# Revit family: Keilhauer_Pact_Bench_Tete_A_Tete_77221
name_source: partatom
category: Furniture
revit_build: Autodesk Revit 2017 (Build: 20160225_1515(x64)
units: mm (PartAtom-declared; Revit-internal decimal feet)

## family parameters
Always vertical = Yes
Cut with Voids When Loaded = No
OmniClass Number = 23.40.70.14.64.11
OmniClass Title = Office Furniture
Room Calculation Point = No
Shared = No
Work Plane-Based = No

## types (10) — shared parameters
Assembly Code = E2020200
Catalog = Pact
Manufacturer = Keilhauer, Corp.
Product Documentation Link = http://www.keilhauer.com
URL = http://www.keilhauer.com

## per-type parameters (varying)
| type | Back Left | Back Right | Config | Description | Front Left | Front Right | Length 1 | Model | Size |
| 84" asymmetrical Tete-A-Tete RAF bench | No | Yes | 4 | Pact 84" asymmetrical Tete-A-Tete RAF bench | Yes | No | 40.61 " | 77235 | 3 |
| 72" asymmetrical Tete-A-Tete RAF bench | Yes | No | 3 | Pact 72" asymmetrical Tete-A-Tete RAF bench | No | Yes | 34.36 " | 77225 | 2 |
| 84" asymmetrical Tete-A-Tete LAF bench | Yes | No | 3 | Pact 84" asymmetrical Tete-A-Tete LAF bench | No | Yes | 40.61 " | 77234 | 3 |
| 72" asymmetrical Tete-A-Tete LAF bench | Yes | No | 1 | Pact 72" asymmetrical Tete-A-Tete LAF bench | No | Yes | 34.36 " | 77224 | 2 |
| 84" Tete-A-Tete short RAF back | No | Yes | 2 | Pact 84" Tete-A-Tete short RAF back | Yes | No | 40.61 " | 77231 | 3 |
| 72" Tete-A-Tete short RAF back | No | Yes | 4 | Pact 72" Tete-A-Tete short RAF back | Yes | No | 34.36 " | 77221 | 2 |
| 57" Tete-A-Tete short RAF back | No | Yes | 2 | Pact 57" Tete-A-Tete short RAF back | Yes | No | 26.86 " | 77211 | 1 |
| 84" Tete-A-Tete short LAF back | Yes | No | 1 | Pact 84" Tete-A-Tete short LAF back | No | Yes | 40.61 " | 77230 | 3 |
| 72" Tete-A-Tete short LAF back | No | Yes | 2 | Pact 72" Tete-A-Tete short LAF back | Yes | No | 34.36 " | 77220 | 2 |
| 57" Tete-A-Tete short LAF back | Yes | No | 1 | Pact 57" Tete-A-Tete short LAF back | No | Yes | 26.86 " | 77210 | 1 |

## geometry (parser evidence)
native form markers: Sweep x7
no freeform markers — native parametric forms only
